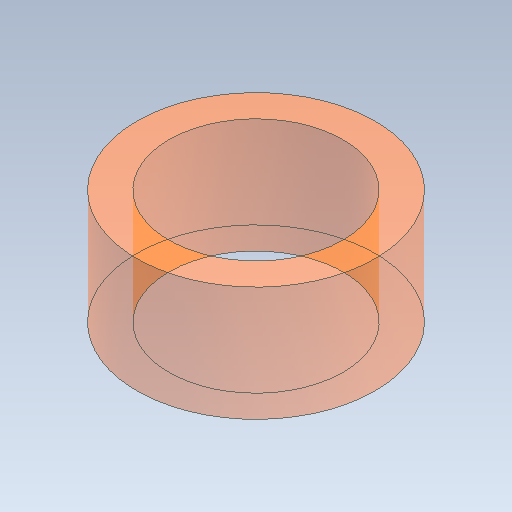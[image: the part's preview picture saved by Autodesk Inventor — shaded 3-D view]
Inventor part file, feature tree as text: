
AUTODESK INVENTOR PART (.ipt)
format: ipt  version: 2020 (Build 240168000, 168)  size: 108,032 bytes
history: native  units: mm
features: extrude x1, sketch x1
ambient origin geometry x8: Origin, YZ Plane, XZ Plane, XY Plane, X Axis, Y Axis, Z Axis, Center Point
bodies: Solid1 (feature_tree)
feature tree (2):
  extrude  "Extrusion1"  Depth=25.0mm
  sketch  "Sketch1"  dims[d0=52.0mm d1=38.0mm d2=25.0mm d3=0.0mm]
